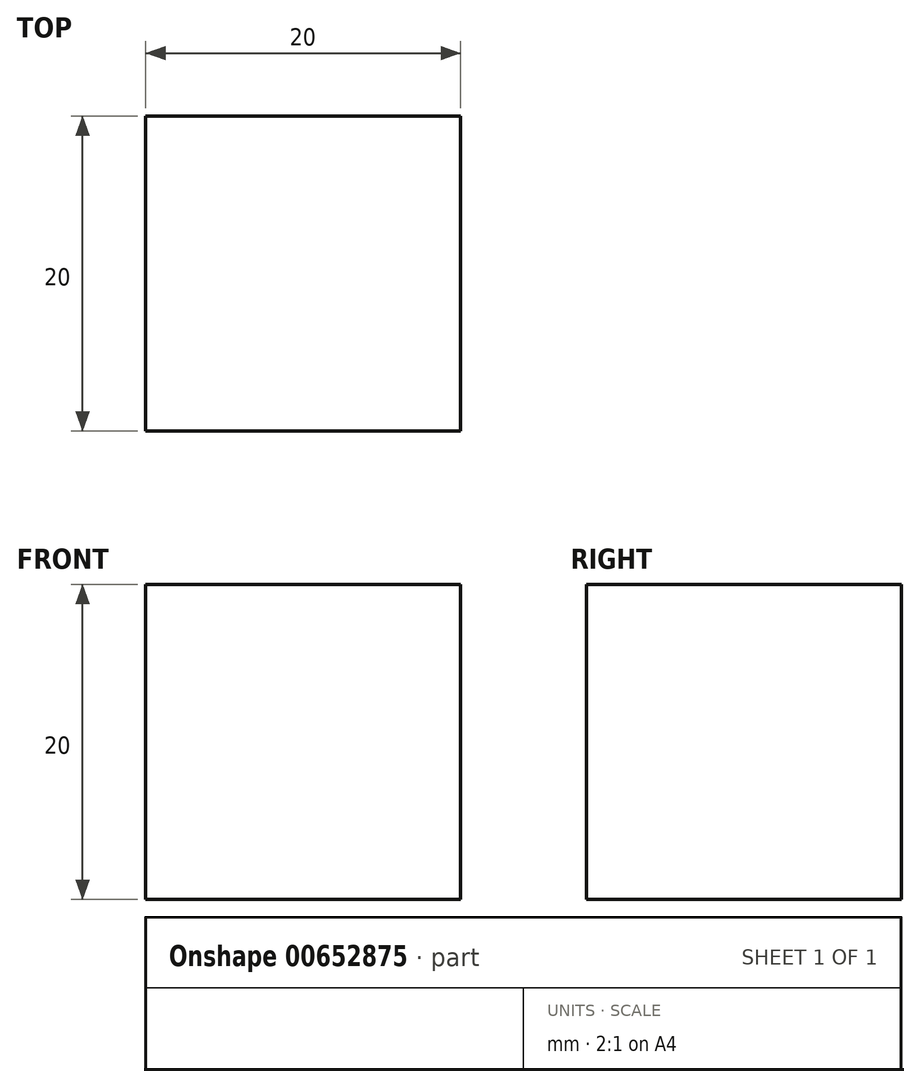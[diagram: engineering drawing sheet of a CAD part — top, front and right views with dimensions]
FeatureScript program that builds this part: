
annotation { "Feature Type Name" : "Feature", "Feature Type Description" : "" }
export const myFeature = defineFeature(function(context is Context, id is Id, definition is map)
    precondition{}
    {
        {
            var Q0;
            Q0=qCreatedBy(makeId("Top.planeOp"),FACE);
            var sketch = newSketch(context, id + "F0", { "sketchPlane" : qUnion([Q0])});
            skLineSegment(sketch, "E0.bottom", {"start": v(-10, -10) * mm, "end": v(10, -10) * mm});
            skLineSegment(sketch, "E0.top", {"start": v(-10, 10) * mm, "end": v(10, 10) * mm});
            skLineSegment(sketch, "E0.left", {"start": v(-10, -10) * mm, "end": v(-10, 10) * mm});
            skLineSegment(sketch, "E0.right", {"start": v(10, -10) * mm, "end": v(10, 10) * mm});
            skPoint(sketch, "E0.middle", {"position": v(0, 0) * mm});
            skSolve(sketch);
        }
        {
            var Q0;
            Q0=makeQuery(id+"F0.imprint","IMPRINT",FACE,{"disambiguationData":[TD([[makeQuery(id+"F0.imprint","IMPRINT",EDGE,{"derivedFrom":sQuery(id+"F0.wireOp",EDGE,"E0.bottom")}),1.0]])]});
            var Q1;
            Q1 = qSketchRegion(id + "F0", true);
            extrude(context, id + "F1", {"entities" : qUnion([Q0, Q1]), "depth" : 20 * mm, "offsetDistance" : 25 * mm});
        }
    });
